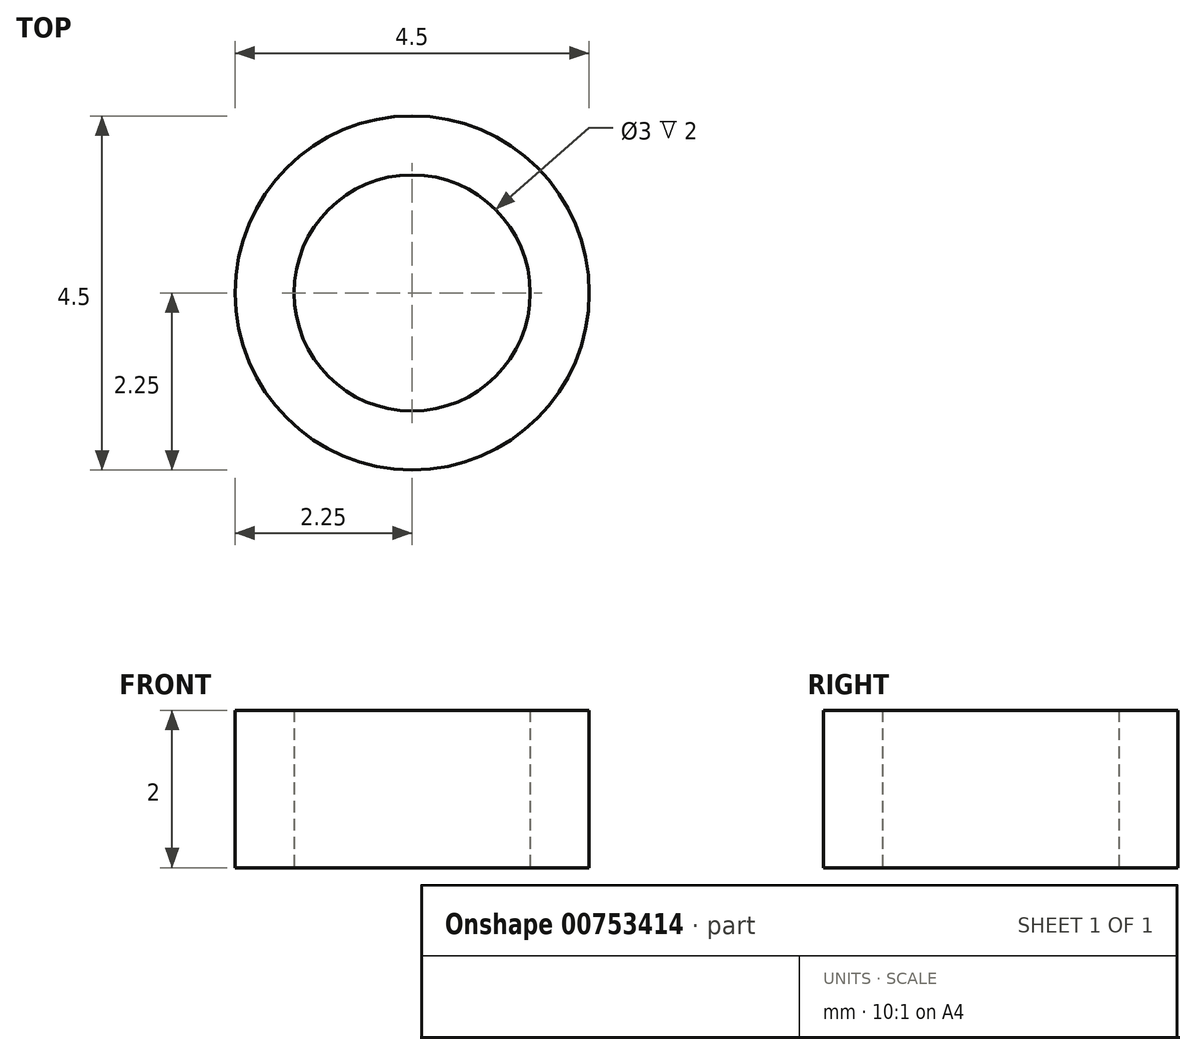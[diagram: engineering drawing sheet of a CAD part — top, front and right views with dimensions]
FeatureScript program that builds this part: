
annotation { "Feature Type Name" : "Feature", "Feature Type Description" : "" }
export const myFeature = defineFeature(function(context is Context, id is Id, definition is map)
    precondition{}
    {
        {
            var Q0;
            Q0=qCreatedBy(makeId("Top.planeOp"),FACE);
            var sketch = newSketch(context, id + "F0", { "sketchPlane" : qUnion([Q0])});
            skCircle(sketch, "E0", {"center": v(0, 0) * mm, "radius": 1.5 * mm});
            skCircle(sketch, "E1", {"center": v(0, 0) * mm, "radius": 2.25 * mm});
            skSolve(sketch);
        }
        {
            var Q0;
            Q0=makeQuery(id+"F0.imprint","IMPRINT",FACE,{"disambiguationData":[TD([[makeQuery(id+"F0.imprint","IMPRINT",EDGE,{"derivedFrom":sQuery(id+"F0.wireOp",EDGE,"E0")}),-1.0]])]});
            extrude(context, id + "F1", {"entities" : qUnion([Q0]), "depth" : 2 * mm, "offsetDistance" : 25 * mm});
        }
    });
